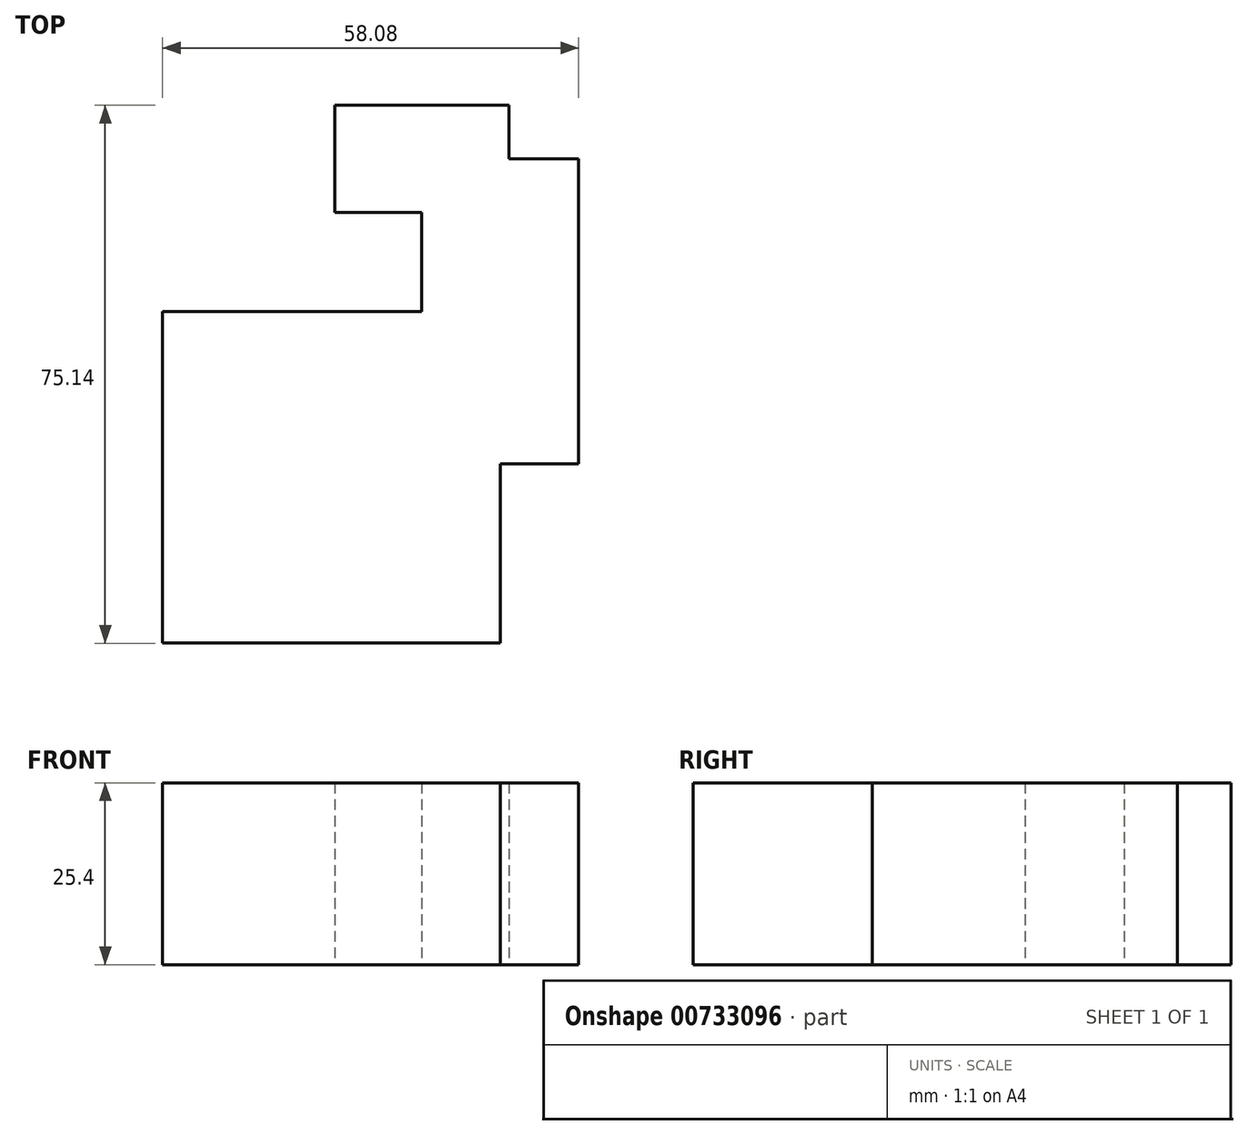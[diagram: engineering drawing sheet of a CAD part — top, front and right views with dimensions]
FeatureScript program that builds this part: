
annotation { "Feature Type Name" : "Feature", "Feature Type Description" : "" }
export const myFeature = defineFeature(function(context is Context, id is Id, definition is map)
    precondition{}
    {
        {
            var Q0;
            Q0=qCreatedBy(makeId("Top.planeOp"), FACE);
            var sketch = newSketch(context, id + "F0", { "sketchPlane" : qUnion([Q0])});
            skLineSegment(sketch, "E0.bottom", {"start": v(-27.97, 23.18) * mm, "end": v(19.17, 23.18) * mm});
            skLineSegment(sketch, "E0.top", {"start": v(-27.97, -23.18) * mm, "end": v(19.17, -23.18) * mm});
            skLineSegment(sketch, "E0.left", {"start": v(-27.97, 23.18) * mm, "end": v(-27.97, -23.18) * mm});
            skLineSegment(sketch, "E0.right", {"start": v(19.17, 23.18) * mm, "end": v(19.17, -23.18) * mm});
            skPoint(sketch, "E0.middle", {"position": v(-4.4, 0) * mm});
            skLineSegment(sketch, "E1.bottom", {"start": v(8.24, 44.48) * mm, "end": v(30.11, 44.48) * mm});
            skLineSegment(sketch, "E1.top", {"start": v(8.24, 1.87) * mm, "end": v(30.11, 1.87) * mm});
            skLineSegment(sketch, "E1.left", {"start": v(8.24, 44.48) * mm, "end": v(8.24, 1.87) * mm});
            skLineSegment(sketch, "E1.right", {"start": v(30.11, 44.48) * mm, "end": v(30.11, 1.87) * mm});
            skPoint(sketch, "E1.middle", {"position": v(19.17, 23.18) * mm});
            skLineSegment(sketch, "E2.bottom", {"start": v(-3.94, 51.96) * mm, "end": v(20.4, 51.96) * mm});
            skLineSegment(sketch, "E2.top", {"start": v(-3.94, 37) * mm, "end": v(20.4, 37) * mm});
            skLineSegment(sketch, "E2.left", {"start": v(-3.94, 51.96) * mm, "end": v(-3.94, 37) * mm});
            skLineSegment(sketch, "E2.right", {"start": v(20.4, 51.96) * mm, "end": v(20.4, 37) * mm});
            skPoint(sketch, "E2.middle", {"position": v(8.24, 44.48) * mm});
            skSolve(sketch);
        }
        {
            var Q0;
            Q0 = qSketchRegion(id + "F0", true);
            extrude(context, id + "F1", {"entities" : qUnion([Q0]), "domain" : OperationDomain.MODEL, "flatOperationType" : FlatOperationType.REMOVE, "depth" : 25.4 * mm, "offsetDistance" : 25.4 * mm});
        }
    });
